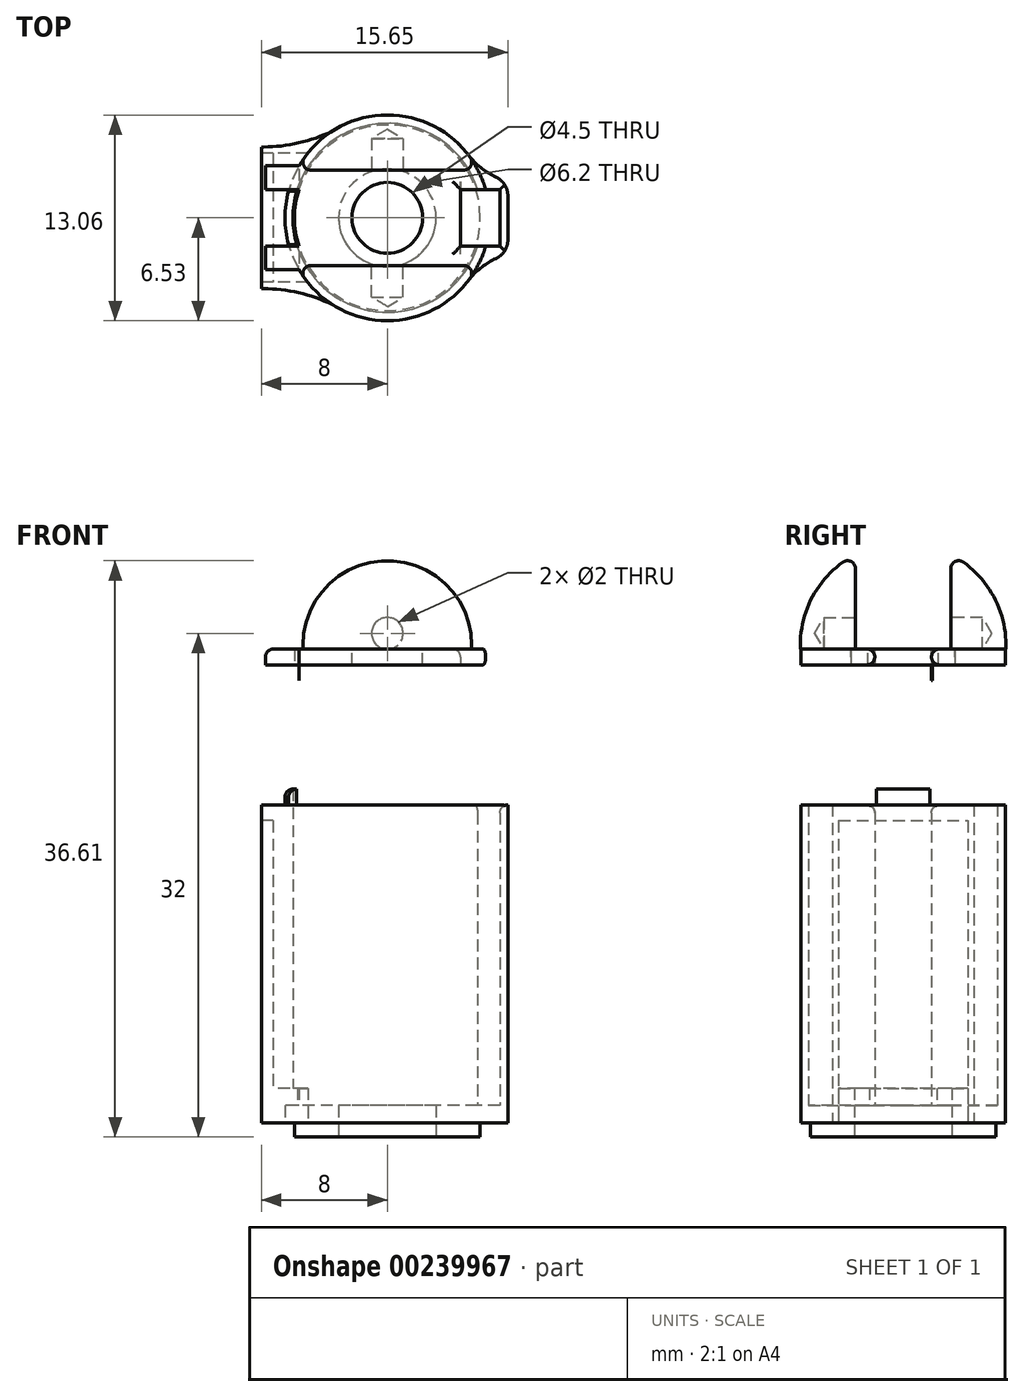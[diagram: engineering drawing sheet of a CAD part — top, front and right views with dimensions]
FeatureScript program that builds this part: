
annotation { "Feature Type Name" : "Feature", "Feature Type Description" : "" }
export const myFeature = defineFeature(function(context is Context, id is Id, definition is map)
    precondition{}
    {
        {
            var Q0;
            Q0=qCreatedBy(makeId("Top.planeOp"),FACE);
            var sketch = newSketch(context, id + "F0", { "sketchPlane" : qUnion([Q0])});
            skCircle(sketch, "E0", {"center": v(0, 0) * mm, "radius": 6 * mm});
            skLineSegment(sketch, "E1.bottom", {"start": v(7.15, 1.8) * mm, "end": v(3.35, 1.8) * mm});
            skLineSegment(sketch, "E1.top", {"start": v(7.15, -1.8) * mm, "end": v(3.35, -1.8) * mm});
            skLineSegment(sketch, "E1.left", {"start": v(7.15, 1.8) * mm, "end": v(7.15, -1.8) * mm});
            skLineSegment(sketch, "E1.right", {"start": v(3.35, 1.8) * mm, "end": v(3.35, -1.8) * mm});
            skCircle(sketch, "E2", {"center": v(0, 0) * mm, "radius": 6.5 * mm});
            skLineSegment(sketch, "E3", {"start": v(6.08, 2.3) * mm, "end": v(7.65, 2.3) * mm});
            skLineSegment(sketch, "E4", {"start": v(7.65, 2.3) * mm, "end": v(7.65, -2.3) * mm});
            skLineSegment(sketch, "E5", {"start": v(7.65, -2.3) * mm, "end": v(6.08, -2.3) * mm});
            skLineSegment(sketch, "E6", {"start": v(3.35, 1.8) * mm, "end": v(-6.25, 1.8) * mm, "construction": true});
            skLineSegment(sketch, "E7", {"start": v(3.35, -1.8) * mm, "end": v(-6.25, -1.8) * mm, "construction": true});
            skLineSegment(sketch, "E8", {"start": v(-6.25, 1.8) * mm, "end": v(-5.72, 1.8) * mm});
            skLineSegment(sketch, "E9", {"start": v(-6.25, -1.8) * mm, "end": v(-5.72, -1.8) * mm});
            skCircle(sketch, "E10", {"center": v(0, 0) * mm, "radius": 5.9 * mm});
            skSolve(sketch);
        }
        {
            var Q0;
            {var subQ2=sQuery(id+"F0.wireOp",EDGE,"E1.bottom");var subQ4=sQuery(id+"F0.wireOp",EDGE,"E0");var subQ5=makeQuery(id+"F0.imprint","INTERSECT",VERTEX,{"derivedFrom":[subQ4,subQ2]});Q0=makeQuery(id+"F0.imprint","IMPRINT",FACE,{"disambiguationData":[TD([[makeQuery(id+"F0.imprint","IMPRINT",EDGE,{"disambiguationData":[TD([[subQ5,-1.0]])],"derivedFrom":subQ4}),-1.0]])]});}
            var Q1;
            {var subQ4=sQuery(id+"F0.wireOp",EDGE,"E1.left");Q1=makeQuery(id+"F0.imprint","IMPRINT",FACE,{"disambiguationData":[TD([[makeQuery(id+"F0.imprint","IMPRINT",EDGE,{"derivedFrom":subQ4}),1.0]])]});}
            var Q2;
            {var subQ0=sQuery(id+"F0.wireOp",EDGE,"E8");Q2=makeQuery(id+"F0.imprint","IMPRINT",FACE,{"disambiguationData":[TD([[makeQuery(id+"F0.imprint","IMPRINT",EDGE,{"derivedFrom":subQ0}),-1.0]])]});}
            var Q3;
            {var subQ2=sQuery(id+"F0.wireOp",EDGE,"E9");Q3=makeQuery(id+"F0.imprint","IMPRINT",FACE,{"disambiguationData":[TD([[makeQuery(id+"F0.imprint","IMPRINT",EDGE,{"derivedFrom":subQ2}),-1.0]])]});}
            extrude(context, id + "F1", {"entities" : qUnion([Q0, Q1, Q2, Q3]), "depth" : 21.1 * mm});
        }
        {
            var Q0;
            {var subQ5=sQuery(id+"F0.wireOp",EDGE,"E1.right");Q0=makeQuery(id+"F0.imprint","IMPRINT",FACE,{"disambiguationData":[TD([[makeQuery(id+"F0.imprint","IMPRINT",EDGE,{"derivedFrom":subQ5}),-1.0]])]});}
            var Q1;
            {var subQ0=sQuery(id+"F0.wireOp",EDGE,"E1.left");Q1=makeQuery(id+"F0.imprint","IMPRINT",FACE,{"disambiguationData":[TD([[makeQuery(id+"F0.imprint","IMPRINT",EDGE,{"derivedFrom":subQ0}),-1.0]])]});}
            var Q2;
            {var subQ0=sQuery(id+"F0.wireOp",EDGE,"E1.bottom");var subQ1=sQuery(id+"F0.wireOp",EDGE,"E0");var subQ2=makeQuery(id+"F0.imprint","INTERSECT",VERTEX,{"derivedFrom":[subQ1,subQ0]});Q2=makeQuery(id+"F0.imprint","IMPRINT",FACE,{"disambiguationData":[TD([[makeQuery(id+"F0.imprint","IMPRINT",EDGE,{"disambiguationData":[TD([[subQ2,1.0]])],"derivedFrom":subQ1}),-1.0]])]});}
            var Q3;
            {var subQ5=sQuery(id+"F0.wireOp",EDGE,"E1.right");Q3=makeQuery(id+"F0.imprint","IMPRINT",FACE,{"disambiguationData":[TD([[makeQuery(id+"F0.imprint","IMPRINT",EDGE,{"derivedFrom":subQ5}),1.0]])]});}
            var Q4;
            {var subQ1=sQuery(id+"F0.wireOp",EDGE,"E0");var subQ8=makeQuery(id+"F0.imprint","INTERSECT",VERTEX,{"derivedFrom":[subQ1,sQuery(id+"F0.wireOp",EDGE,"E8")]});Q4=makeQuery(id+"F0.imprint","IMPRINT",FACE,{"disambiguationData":[TD([[makeQuery(id+"F0.imprint","IMPRINT",EDGE,{"disambiguationData":[TD([[subQ8,1.0]])],"derivedFrom":subQ1}),1.0]])]});}
            var Q5;
            {var subQ0=sQuery(id+"F0.wireOp",EDGE,"E1.bottom");var subQ1=sQuery(id+"F0.wireOp",EDGE,"E0");var subQ2=makeQuery(id+"F0.imprint","INTERSECT",VERTEX,{"derivedFrom":[subQ1,subQ0]});Q5=makeQuery(id+"F0.imprint","IMPRINT",FACE,{"disambiguationData":[TD([[makeQuery(id+"F0.imprint","IMPRINT",EDGE,{"disambiguationData":[TD([[subQ2,1.0]])],"derivedFrom":subQ1}),1.0]])]});}
            extrude(context, id + "F2", {"entities" : qUnion([Q0, Q1, Q2, Q3, Q4, Q5]), "operationType" : NewBodyOperationType.ADD, "depth" : 2 * mm});
        }
        {
            var Q0;
            {var subQ0=sQuery(id+"F0.wireOp",EDGE,"E1.left");Q0=makeQuery(id+"F0.imprint","IMPRINT",FACE,{"disambiguationData":[TD([[makeQuery(id+"F0.imprint","IMPRINT",EDGE,{"derivedFrom":subQ0}),-1.0]])]});}
            var Q1;
            {var subQ7=sQuery(id+"F0.wireOp",EDGE,"E1.left");Q1=makeQuery(id+"F0.imprint","IMPRINT",FACE,{"disambiguationData":[TD([[makeQuery(id+"F0.imprint","IMPRINT",EDGE,{"derivedFrom":subQ7}),1.0]])]});}
            extrude(context, id + "F3", {"entities" : qUnion([Q0, Q1]), "operationType" : NewBodyOperationType.REMOVE, "depth" : 0.9 * mm});
        }
        {
            var Q0;
            Q0=sQuery(id+"F0.wireOp",VERTEX,"E0.center");
            var Q1;
            Q1=makeQuery(id+"F1.opExtrude","SWEPT_BODY",BODY,{"disambiguationData":[OSD([sQuery(id+"F0.wireOp",EDGE,"E0"),sQuery(id+"F0.wireOp",EDGE,"4U9qkods-u3rM-atFx-P1sS-Y80TmgSaHfty.bottom"),sQuery(id+"F0.wireOp",EDGE,"4U9qkods-u3rM-atFx-P1sS-Y80TmgSaHfty.top"),sQuery(id+"F0.wireOp",EDGE,"4U9qkods-u3rM-atFx-P1sS-Y80TmgSaHfty.left"),sQuery(id+"F0.wireOp",EDGE,"4U9qkods-u3rM-atFx-P1sS-Y80TmgSaHfty.right"),sQuery(id+"F0.wireOp",EDGE,"mv0gvk0f-OwlG-QK1v-DSVR-qk8BXU6s7eKN"),sQuery(id+"F0.wireOp",EDGE,"3gOzF7jk-Ag0X-tEXh-jwYR-98HZdRz7N0tB"),sQuery(id+"F0.wireOp",EDGE,"9Uo2PhHU-4JkB-lCzV-Wcka-mTuiKmUsuITT")])]});
            hole(context, id + "F4", {"style" : HoleStyle.SIMPLE, "endStyle" : HoleEndStyle.THROUGH, "oppositeDirection" : true, "holeDiameter" : 6.2 * mm, "locations" : qUnion([Q0]), "scope" : qUnion([Q1]), "isTappedThrough" : true});
        }
        {
            var Q0;
            Q0=qCreatedBy(makeId("Top.planeOp"),FACE);
            cPlane(context, id + "F5", {"entities" : qUnion([Q0]), "cplaneType" : CPlaneType.OFFSET, "offset" : 30 * mm, "width" : 150 * mm, "height" : 150 * mm});
        }
        {
            var Q0;
            Q0=qCreatedBy(id+"F5.planeOp",FACE);
            var sketch = newSketch(context, id + "F6", { "sketchPlane" : qUnion([Q0])});
            skCircle(sketch, "E11", {"center": v(0, 0) * mm, "radius": 5.9 * mm});
            skCircle(sketch, "E12", {"center": v(0, 0) * mm, "radius": 6.5 * mm});
            skLineSegment(sketch, "E13", {"start": v(4.65, 1.8) * mm, "end": v(6.25, 1.8) * mm});
            skLineSegment(sketch, "E14", {"start": v(4.65, -1.8) * mm, "end": v(6.25, -1.8) * mm});
            skLineSegment(sketch, "E15", {"start": v(7.15, 1.8) * mm, "end": v(-6.25, 1.8) * mm, "construction": true});
            skLineSegment(sketch, "E16", {"start": v(7.15, -1.8) * mm, "end": v(-6.25, -1.8) * mm, "construction": true});
            skLineSegment(sketch, "E17", {"start": v(-6.25, 1.8) * mm, "end": v(-5.62, 1.8) * mm});
            skLineSegment(sketch, "E18", {"start": v(-6.25, -1.8) * mm, "end": v(-5.62, -1.8) * mm});
            skLineSegment(sketch, "E19", {"start": v(4.65, 1.8) * mm, "end": v(4.65, -1.8) * mm});
            skCircle(sketch, "E20", {"center": v(0, 0) * mm, "radius": 4.5 * mm});
            skLineSegment(sketch, "E21.bottom", {"start": v(-7.75, 1.8) * mm, "end": v(-6.25, 1.8) * mm});
            skLineSegment(sketch, "E21.top", {"start": v(-7.75, -1.8) * mm, "end": v(-6.25, -1.8) * mm});
            skLineSegment(sketch, "E21.left", {"start": v(-7.75, 1.8) * mm, "end": v(-7.75, -1.8) * mm});
            skLineSegment(sketch, "E21.right", {"start": v(-6.25, 1.8) * mm, "end": v(-6.25, -1.8) * mm});
            skLineSegment(sketch, "E22.bottom", {"start": v(-7.75, 1.8) * mm, "end": v(-5.6, 1.8) * mm});
            skLineSegment(sketch, "E22.top", {"start": v(-7.75, 3.3) * mm, "end": v(-5.6, 3.3) * mm});
            skLineSegment(sketch, "E22.left", {"start": v(-7.75, 1.8) * mm, "end": v(-7.75, 3.3) * mm});
            skLineSegment(sketch, "E22.right", {"start": v(-5.6, 1.8) * mm, "end": v(-5.6, 3.3) * mm});
            skLineSegment(sketch, "E23.bottom", {"start": v(-7.75, -1.8) * mm, "end": v(-5.6, -1.8) * mm});
            skLineSegment(sketch, "E23.top", {"start": v(-7.75, -3.3) * mm, "end": v(-5.6, -3.3) * mm});
            skLineSegment(sketch, "E23.left", {"start": v(-7.75, -1.8) * mm, "end": v(-7.75, -3.3) * mm});
            skLineSegment(sketch, "E23.right", {"start": v(-5.6, -1.8) * mm, "end": v(-5.6, -3.3) * mm});
            skSolve(sketch);
        }
        {
            var Q0;
            {var subQ0=sQuery(id+"F6.wireOp",EDGE,"E22.right");var subQ1=sQuery(id+"F6.wireOp",EDGE,"E11");var subQ2=makeQuery(id+"F6.imprint","INTERSECT",VERTEX,{"derivedFrom":[subQ1,subQ0]});Q0=makeQuery(id+"F6.imprint","IMPRINT",FACE,{"disambiguationData":[TD([[makeQuery(id+"F6.imprint","IMPRINT",EDGE,{"disambiguationData":[TD([[subQ2,1.0]])],"derivedFrom":subQ1}),-1.0]])]});}
            var Q1;
            {var subQ0=sQuery(id+"F6.wireOp",EDGE,"E23.right");var subQ1=sQuery(id+"F6.wireOp",EDGE,"E11");var subQ2=makeQuery(id+"F6.imprint","INTERSECT",VERTEX,{"derivedFrom":[subQ1,subQ0]});Q1=makeQuery(id+"F6.imprint","IMPRINT",FACE,{"disambiguationData":[TD([[makeQuery(id+"F6.imprint","IMPRINT",EDGE,{"disambiguationData":[TD([[subQ2,-1.0]])],"derivedFrom":subQ1}),-1.0]])]});}
            var Q2;
            {var subQ0=sQuery(id+"F6.wireOp",EDGE,"E22.right");var subQ1=sQuery(id+"F6.wireOp",EDGE,"E11");var subQ2=makeQuery(id+"F6.imprint","INTERSECT",VERTEX,{"derivedFrom":[subQ1,subQ0]});Q2=makeQuery(id+"F6.imprint","IMPRINT",FACE,{"disambiguationData":[TD([[makeQuery(id+"F6.imprint","IMPRINT",EDGE,{"disambiguationData":[TD([[subQ2,-1.0]])],"derivedFrom":subQ1}),-1.0]])]});}
            var Q3;
            {var subQ0=sQuery(id+"F6.wireOp",EDGE,"E23.bottom");var subQ1=sQuery(id+"F6.wireOp",EDGE,"E11");var subQ2=makeQuery(id+"F6.imprint","INTERSECT",VERTEX,{"derivedFrom":[subQ1,subQ0]});Q3=makeQuery(id+"F6.imprint","IMPRINT",FACE,{"disambiguationData":[TD([[makeQuery(id+"F6.imprint","IMPRINT",EDGE,{"disambiguationData":[TD([[subQ2,-1.0]])],"derivedFrom":subQ1}),-1.0]])]});}
            var Q4;
            {var subQ0=sQuery(id+"F6.wireOp",EDGE,"E22.right");var subQ1=sQuery(id+"F6.wireOp",EDGE,"E11");var subQ2=makeQuery(id+"F6.imprint","INTERSECT",VERTEX,{"derivedFrom":[subQ1,subQ0]});Q4=makeQuery(id+"F6.imprint","IMPRINT",FACE,{"disambiguationData":[TD([[makeQuery(id+"F6.imprint","IMPRINT",EDGE,{"disambiguationData":[TD([[subQ2,1.0]])],"derivedFrom":subQ1}),-1.0]])]});}
            var Q5;
            {var subQ0=sQuery(id+"F6.wireOp",EDGE,"E23.right");var subQ1=sQuery(id+"F6.wireOp",EDGE,"E11");var subQ2=makeQuery(id+"F6.imprint","INTERSECT",VERTEX,{"derivedFrom":[subQ1,subQ0]});Q5=makeQuery(id+"F6.imprint","IMPRINT",FACE,{"disambiguationData":[TD([[makeQuery(id+"F6.imprint","IMPRINT",EDGE,{"disambiguationData":[TD([[subQ2,-1.0]])],"derivedFrom":subQ1}),-1.0]])]});}
            var Q6;
            {var subQ0=sQuery(id+"F6.wireOp",EDGE,"E22.right");var subQ1=sQuery(id+"F6.wireOp",EDGE,"E11");var subQ2=makeQuery(id+"F6.imprint","INTERSECT",VERTEX,{"derivedFrom":[subQ1,subQ0]});Q6=makeQuery(id+"F6.imprint","IMPRINT",FACE,{"disambiguationData":[TD([[makeQuery(id+"F6.imprint","IMPRINT",EDGE,{"disambiguationData":[TD([[subQ2,-1.0]])],"derivedFrom":subQ1}),-1.0]])]});}
            var Q7;
            {var subQ0=sQuery(id+"F6.wireOp",EDGE,"E23.bottom");var subQ1=sQuery(id+"F6.wireOp",EDGE,"E11");var subQ2=makeQuery(id+"F6.imprint","INTERSECT",VERTEX,{"derivedFrom":[subQ1,subQ0]});Q7=makeQuery(id+"F6.imprint","IMPRINT",FACE,{"disambiguationData":[TD([[makeQuery(id+"F6.imprint","IMPRINT",EDGE,{"disambiguationData":[TD([[subQ2,-1.0]])],"derivedFrom":subQ1}),-1.0]])]});}
            var Q8;
            {var subQ5=sQuery(id+"F6.wireOp",EDGE,"E19");Q8=makeQuery(id+"F6.imprint","IMPRINT",FACE,{"disambiguationData":[TD([[makeQuery(id+"F6.imprint","IMPRINT",EDGE,{"derivedFrom":subQ5}),-1.0]])]});}
            var Q9;
            {var subQ5=sQuery(id+"F6.wireOp",EDGE,"E19");Q9=makeQuery(id+"F6.imprint","IMPRINT",FACE,{"disambiguationData":[TD([[makeQuery(id+"F6.imprint","IMPRINT",EDGE,{"derivedFrom":subQ5}),-1.0]])]});}
            var Q10;
            {var subQ5=sQuery(id+"F6.wireOp",EDGE,"E19");Q10=makeQuery(id+"F6.imprint","IMPRINT",FACE,{"disambiguationData":[TD([[makeQuery(id+"F6.imprint","IMPRINT",EDGE,{"derivedFrom":subQ5}),-1.0]])]});}
            var Q11;
            {var subQ5=sQuery(id+"F6.wireOp",EDGE,"E19");Q11=makeQuery(id+"F6.imprint","IMPRINT",FACE,{"disambiguationData":[TD([[makeQuery(id+"F6.imprint","IMPRINT",EDGE,{"derivedFrom":subQ5}),-1.0]])]});}
            var Q12;
            {var subQ5=sQuery(id+"F6.wireOp",EDGE,"E19");Q12=makeQuery(id+"F6.imprint","IMPRINT",FACE,{"disambiguationData":[TD([[makeQuery(id+"F6.imprint","IMPRINT",EDGE,{"derivedFrom":subQ5}),-1.0]])]});}
            var Q13;
            Q13=makeQuery(id+"F6.imprint","IMPRINT",FACE,{"disambiguationData":[TD([[makeQuery(id+"F6.imprint","IMPRINT",EDGE,{"derivedFrom":sQuery(id+"F6.wireOp",EDGE,"E20")}),1.0]])]});
            var Q14;
            {var subQ0=sQuery(id+"F6.wireOp",EDGE,"E22.right");var subQ1=sQuery(id+"F6.wireOp",EDGE,"E11");var subQ2=makeQuery(id+"F6.imprint","INTERSECT",VERTEX,{"derivedFrom":[subQ1,subQ0]});Q14=makeQuery(id+"F6.imprint","IMPRINT",FACE,{"disambiguationData":[TD([[makeQuery(id+"F6.imprint","IMPRINT",EDGE,{"disambiguationData":[TD([[subQ2,1.0]])],"derivedFrom":subQ1}),-1.0]])]});}
            var Q15;
            {var subQ0=sQuery(id+"F6.wireOp",EDGE,"E23.right");var subQ1=sQuery(id+"F6.wireOp",EDGE,"E11");var subQ2=makeQuery(id+"F6.imprint","INTERSECT",VERTEX,{"derivedFrom":[subQ1,subQ0]});Q15=makeQuery(id+"F6.imprint","IMPRINT",FACE,{"disambiguationData":[TD([[makeQuery(id+"F6.imprint","IMPRINT",EDGE,{"disambiguationData":[TD([[subQ2,-1.0]])],"derivedFrom":subQ1}),-1.0]])]});}
            var Q16;
            {var subQ0=sQuery(id+"F6.wireOp",EDGE,"E22.right");var subQ1=sQuery(id+"F6.wireOp",EDGE,"E11");var subQ2=makeQuery(id+"F6.imprint","INTERSECT",VERTEX,{"derivedFrom":[subQ1,subQ0]});Q16=makeQuery(id+"F6.imprint","IMPRINT",FACE,{"disambiguationData":[TD([[makeQuery(id+"F6.imprint","IMPRINT",EDGE,{"disambiguationData":[TD([[subQ2,-1.0]])],"derivedFrom":subQ1}),-1.0]])]});}
            var Q17;
            {var subQ0=sQuery(id+"F6.wireOp",EDGE,"E23.bottom");var subQ1=sQuery(id+"F6.wireOp",EDGE,"E11");var subQ2=makeQuery(id+"F6.imprint","INTERSECT",VERTEX,{"derivedFrom":[subQ1,subQ0]});Q17=makeQuery(id+"F6.imprint","IMPRINT",FACE,{"disambiguationData":[TD([[makeQuery(id+"F6.imprint","IMPRINT",EDGE,{"disambiguationData":[TD([[subQ2,-1.0]])],"derivedFrom":subQ1}),-1.0]])]});}
            var Q18;
            {var subQ3=sQuery(id+"F6.wireOp",EDGE,"E22.top");Q18=makeQuery(id+"F6.imprint","IMPRINT",FACE,{"disambiguationData":[TD([[makeQuery(id+"F6.imprint","IMPRINT",EDGE,{"derivedFrom":subQ3}),-1.0]])]});}
            var Q19;
            {var subQ0=sQuery(id+"F6.wireOp",EDGE,"E22.right");var subQ1=sQuery(id+"F6.wireOp",EDGE,"E11");var subQ2=makeQuery(id+"F6.imprint","INTERSECT",VERTEX,{"derivedFrom":[subQ1,subQ0]});Q19=makeQuery(id+"F6.imprint","IMPRINT",FACE,{"disambiguationData":[TD([[makeQuery(id+"F6.imprint","IMPRINT",EDGE,{"disambiguationData":[TD([[subQ2,1.0]])],"derivedFrom":subQ1}),-1.0]])]});}
            var Q20;
            {var subQ0=sQuery(id+"F6.wireOp",EDGE,"E22.right");var subQ1=sQuery(id+"F6.wireOp",EDGE,"E11");var subQ2=makeQuery(id+"F6.imprint","INTERSECT",VERTEX,{"derivedFrom":[subQ1,subQ0]});Q20=makeQuery(id+"F6.imprint","IMPRINT",FACE,{"disambiguationData":[TD([[makeQuery(id+"F6.imprint","IMPRINT",EDGE,{"disambiguationData":[TD([[subQ2,-1.0]])],"derivedFrom":subQ1}),-1.0]])]});}
            var Q21;
            {var subQ0=sQuery(id+"F6.wireOp",EDGE,"E23.bottom");var subQ1=sQuery(id+"F6.wireOp",EDGE,"E11");var subQ2=makeQuery(id+"F6.imprint","INTERSECT",VERTEX,{"derivedFrom":[subQ1,subQ0]});Q21=makeQuery(id+"F6.imprint","IMPRINT",FACE,{"disambiguationData":[TD([[makeQuery(id+"F6.imprint","IMPRINT",EDGE,{"disambiguationData":[TD([[subQ2,-1.0]])],"derivedFrom":subQ1}),-1.0]])]});}
            var Q22;
            {var subQ0=sQuery(id+"F6.wireOp",EDGE,"E23.right");var subQ1=sQuery(id+"F6.wireOp",EDGE,"E11");var subQ2=makeQuery(id+"F6.imprint","INTERSECT",VERTEX,{"derivedFrom":[subQ1,subQ0]});Q22=makeQuery(id+"F6.imprint","IMPRINT",FACE,{"disambiguationData":[TD([[makeQuery(id+"F6.imprint","IMPRINT",EDGE,{"disambiguationData":[TD([[subQ2,-1.0]])],"derivedFrom":subQ1}),-1.0]])]});}
            var Q23;
            {var subQ3=sQuery(id+"F6.wireOp",EDGE,"E23.top");Q23=makeQuery(id+"F6.imprint","IMPRINT",FACE,{"disambiguationData":[TD([[makeQuery(id+"F6.imprint","IMPRINT",EDGE,{"derivedFrom":subQ3}),1.0]])]});}
            var Q24;
            {var subQ0=sQuery(id+"F6.wireOp",EDGE,"E22.right");var subQ1=sQuery(id+"F6.wireOp",EDGE,"E11");var subQ2=makeQuery(id+"F6.imprint","INTERSECT",VERTEX,{"derivedFrom":[subQ1,subQ0]});Q24=makeQuery(id+"F6.imprint","IMPRINT",FACE,{"disambiguationData":[TD([[makeQuery(id+"F6.imprint","IMPRINT",EDGE,{"disambiguationData":[TD([[subQ2,-1.0]])],"derivedFrom":subQ1}),1.0]])]});}
            var Q25;
            {var subQ0=sQuery(id+"F6.wireOp",EDGE,"E23.bottom");var subQ1=sQuery(id+"F6.wireOp",EDGE,"E11");var subQ2=makeQuery(id+"F6.imprint","INTERSECT",VERTEX,{"derivedFrom":[subQ1,subQ0]});Q25=makeQuery(id+"F6.imprint","IMPRINT",FACE,{"disambiguationData":[TD([[makeQuery(id+"F6.imprint","IMPRINT",EDGE,{"disambiguationData":[TD([[subQ2,-1.0]])],"derivedFrom":subQ1}),1.0]])]});}
            extrude(context, id + "F7", {"entities" : qUnion([Q0, Q1, Q2, Q3, Q4, Q5, Q6, Q7, Q8, Q9, Q10, Q11, Q12, Q13, Q14, Q15, Q16, Q17, Q18, Q19, Q20, Q21, Q22, Q23, Q24, Q25]), "depth" : 1 * mm});
        }
        {
            var Q0;
            {var subQ0=sQuery(id+"F6.wireOp",EDGE,"4l1vRjtD-Y7ke-iHX6-YueY-vymgdgJSGHIw");Q0=makeQuery(id+"F6.imprint","IMPRINT",FACE,{"disambiguationData":[TD([[makeQuery(id+"F6.imprint","IMPRINT",EDGE,{"derivedFrom":subQ0}),-1.0]])]});}
            var Q1;
            {var subQ1=sQuery(id+"F6.wireOp",EDGE,"E11");var subQ9=makeQuery(id+"F6.imprint","INTERSECT",VERTEX,{"derivedFrom":[subQ1,sQuery(id+"F6.wireOp",EDGE,"E17")]});Q1=makeQuery(id+"F6.imprint","IMPRINT",FACE,{"disambiguationData":[TD([[makeQuery(id+"F6.imprint","IMPRINT",EDGE,{"disambiguationData":[TD([[subQ9,1.0]])],"derivedFrom":subQ1}),1.0]])]});}
            extrude(context, id + "F8", {"entities" : qUnion([Q0, Q1]), "operationType" : NewBodyOperationType.ADD, "oppositeDirection" : true, "depth" : 1 * mm});
        }
        {
            var Q0;
            Q0=makeQuery(id+"F7.opExtrude","CAP_FACE",FACE,{"disambiguationData":[OSD([sQuery(id+"F6.wireOp",EDGE,"E12")])],"isStart":false});
            var sketch = newSketch(context, id + "F9", { "sketchPlane" : qUnion([Q0])});
            skPoint(sketch, "E24", {"position": v(0, 0) * mm});
            skLineSegment(sketch, "E25.bottom", {"start": v(-5.75, 6.53) * mm, "end": v(5.75, 6.53) * mm});
            skLineSegment(sketch, "E25.top", {"start": v(-5.75, 3.03) * mm, "end": v(5.75, 3.03) * mm});
            skLineSegment(sketch, "E25.left", {"start": v(-5.75, 6.53) * mm, "end": v(-5.75, 3.03) * mm});
            skLineSegment(sketch, "E25.right", {"start": v(5.75, 6.53) * mm, "end": v(5.75, 3.03) * mm});
            skLineSegment(sketch, "E26", {"start": v(0, 6.56) * mm, "end": v(0, -6.53) * mm, "construction": true});
            skPoint(sketch, "E27", {"position": v(0, 3.03) * mm});
            skLineSegment(sketch, "E28.MirrorCS", {"start": v(-5.75, -6.53) * mm, "end": v(5.75, -6.53) * mm});
            skLineSegment(sketch, "E29.MirrorCS", {"start": v(-5.75, -3.03) * mm, "end": v(5.75, -3.03) * mm});
            skLineSegment(sketch, "E30.MirrorCS", {"start": v(-5.75, -6.53) * mm, "end": v(-5.75, -3.03) * mm});
            skLineSegment(sketch, "E31.MirrorCS", {"start": v(5.75, -6.53) * mm, "end": v(5.75, -3.03) * mm});
            skSolve(sketch);
        }
        {
            var Q0;
            Q0=sQuery(id+"F9.wireOp",VERTEX,"E24");
            var Q1;
            Q1=makeQuery(id+"F7.opExtrude","SWEPT_BODY",BODY,{"disambiguationData":[OSD([sQuery(id+"F6.wireOp",EDGE,"E12")])]});
            hole(context, id + "F10", {"style" : HoleStyle.SIMPLE, "endStyle" : HoleEndStyle.THROUGH, "holeDiameter" : 4.5 * mm, "locations" : qUnion([Q0]), "scope" : qUnion([Q1]), "isTappedThrough" : true});
        }
        {
            var Q0;
            Q0=makeQuery(id+"F1.opExtrude","CAP_FACE",FACE,{"disambiguationData":[OSD([sQuery(id+"F0.wireOp",EDGE,"E0"),sQuery(id+"F0.wireOp",EDGE,"E1.bottom"),sQuery(id+"F0.wireOp",EDGE,"E1.top"),sQuery(id+"F0.wireOp",EDGE,"E1.left"),sQuery(id+"F0.wireOp",EDGE,"E2"),sQuery(id+"F0.wireOp",EDGE,"E3"),sQuery(id+"F0.wireOp",EDGE,"E4"),sQuery(id+"F0.wireOp",EDGE,"E5")])],"isStart":false});
            var sketch = newSketch(context, id + "F11", { "sketchPlane" : qUnion([Q0])});
            skLineSegment(sketch, "E32", {"start": v(-6.27, 1.7) * mm, "end": v(-5.75, 1.7) * mm});
            skArc(sketch, "E33", {"start": v(-6.27, 1.7) * mm, "mid": v(-6.5, 0) * mm, "end": v(-6.27, -1.7) * mm});
            skArc(sketch, "E34", {"start": v(-5.75, 1.7) * mm, "mid": v(-6, 0) * mm, "end": v(-5.75, -1.7) * mm});
            skLineSegment(sketch, "E35", {"start": v(-6.27, -1.7) * mm, "end": v(-5.75, -1.7) * mm});
            skLineSegment(sketch, "E36", {"start": v(7.15, 1.8) * mm, "end": v(7.15, 2.3) * mm});
            skLineSegment(sketch, "E37", {"start": v(7.15, -1.8) * mm, "end": v(7.15, -2.3) * mm});
            skSolve(sketch);
        }
        {
            var Q0;
            Q0=makeQuery(id+"F11.imprint","IMPRINT",FACE,{"disambiguationData":[TD([[makeQuery(id+"F11.imprint","IMPRINT",EDGE,{"derivedFrom":sQuery(id+"F11.wireOp",EDGE,"E32")}),-1.0]])]});
            extrude(context, id + "F12", {"entities" : qUnion([Q0]), "operationType" : NewBodyOperationType.ADD, "depth" : 1 * mm});
        }
        {
            var Q0;
            {var subQ1=sQuery(id+"F9.wireOp",EDGE,"E25.top");Q0=makeQuery(id+"F9.imprint","IMPRINT",FACE,{"disambiguationData":[TD([[makeQuery(id+"F9.imprint","IMPRINT",EDGE,{"derivedFrom":subQ1}),1.0]])]});}
            var Q1;
            {var subQ1=sQuery(id+"F9.wireOp",EDGE,"E29.MirrorCS");Q1=makeQuery(id+"F9.imprint","IMPRINT",FACE,{"disambiguationData":[TD([[makeQuery(id+"F9.imprint","IMPRINT",EDGE,{"derivedFrom":subQ1}),-1.0]])]});}
            var Q2;
            {var subQ0=sQuery(id+"F9.wireOp",EDGE,"E30.MirrorCS");var subQ1=sQuery(id+"F9.wireOp",EDGE,"E28.MirrorCS");var subQ2=makeQuery(id+"F9.imprint","INTERSECT",VERTEX,{"derivedFrom":[subQ1,subQ0]});Q2=makeQuery(id+"F9.imprint","IMPRINT",FACE,{"disambiguationData":[TD([[makeQuery(id+"F9.imprint","IMPRINT",EDGE,{"disambiguationData":[TD([[subQ2,-1.0]])],"derivedFrom":subQ1}),1.0]])]});}
            var Q3;
            {var subQ0=sQuery(id+"F9.wireOp",EDGE,"E31.MirrorCS");var subQ1=sQuery(id+"F9.wireOp",EDGE,"E28.MirrorCS");var subQ2=makeQuery(id+"F9.imprint","INTERSECT",VERTEX,{"derivedFrom":[subQ1,subQ0]});Q3=makeQuery(id+"F9.imprint","IMPRINT",FACE,{"disambiguationData":[TD([[makeQuery(id+"F9.imprint","IMPRINT",EDGE,{"disambiguationData":[TD([[subQ2,1.0]])],"derivedFrom":subQ1}),1.0]])]});}
            var Q4;
            {var subQ0=sQuery(id+"F9.wireOp",EDGE,"E25.right");var subQ1=sQuery(id+"F9.wireOp",EDGE,"E25.bottom");var subQ2=makeQuery(id+"F9.imprint","INTERSECT",VERTEX,{"derivedFrom":[subQ1,subQ0]});Q4=makeQuery(id+"F9.imprint","IMPRINT",FACE,{"disambiguationData":[TD([[makeQuery(id+"F9.imprint","IMPRINT",EDGE,{"disambiguationData":[TD([[subQ2,1.0]])],"derivedFrom":subQ1}),-1.0]])]});}
            var Q5;
            {var subQ0=sQuery(id+"F9.wireOp",EDGE,"E25.left");var subQ1=sQuery(id+"F9.wireOp",EDGE,"E25.bottom");var subQ2=makeQuery(id+"F9.imprint","INTERSECT",VERTEX,{"derivedFrom":[subQ1,subQ0]});Q5=makeQuery(id+"F9.imprint","IMPRINT",FACE,{"disambiguationData":[TD([[makeQuery(id+"F9.imprint","IMPRINT",EDGE,{"disambiguationData":[TD([[subQ2,-1.0]])],"derivedFrom":subQ1}),-1.0]])]});}
            extrude(context, id + "F13", {"entities" : qUnion([Q0, Q1, Q2, Q3, Q4, Q5]), "operationType" : NewBodyOperationType.ADD, "depth" : 6 * mm});
        }
        {
            var Q0;
            Q0=makeQuery(id+"F13.opExtrude","CAP_EDGE",EDGE,{"disambiguationData":[OSD([sQuery(id+"F9.wireOp",EDGE,"E30.MirrorCS")])],"isStart":false});
            var Q1;
            Q1=makeQuery(id+"F13.opExtrude","CAP_EDGE",EDGE,{"disambiguationData":[OSD([sQuery(id+"F9.wireOp",EDGE,"E31.MirrorCS")])],"isStart":false});
            var Q2;
            Q2=makeQuery(id+"F13.opExtrude","CAP_EDGE",EDGE,{"disambiguationData":[OSD([sQuery(id+"F9.wireOp",EDGE,"E25.left")])],"isStart":false});
            var Q3;
            Q3=makeQuery(id+"F13.opExtrude","CAP_EDGE",EDGE,{"disambiguationData":[OSD([sQuery(id+"F9.wireOp",EDGE,"E25.right")])],"isStart":false});
            fillet(context, id + "F14", {"entities" : qUnion([Q0, Q1, Q2, Q3]), "radius" : 5.75 * mm, "tangentPropagation" : true, "allowEdgeOverflow" : false});
        }
        {
            var Q0;
            Q0=makeQuery(id+"F13.opExtrude","SWEPT_FACE",FACE,{"disambiguationData":[OSD([sQuery(id+"F9.wireOp",EDGE,"E28.MirrorCS")])]});
            var sketch = newSketch(context, id + "F15", { "sketchPlane" : qUnion([Q0])});
            skPoint(sketch, "E38", {"position": v(0, 32) * mm});
            skCircle(sketch, "E39", {"center": v(0, 32) * mm, "radius": 1 * mm, "construction": true});
            skSolve(sketch);
        }
        {
            var Q0;
            Q0=makeQuery(id+"F1.opExtrude","SWEPT_EDGE",EDGE,{"disambiguationData":[OSD([sQuery(id+"F0.wireOp",EDGE,"E2"),sQuery(id+"F0.wireOp",EDGE,"E5")])]});
            var Q1;
            Q1=makeQuery(id+"F1.opExtrude","SWEPT_EDGE",EDGE,{"disambiguationData":[OSD([sQuery(id+"F0.wireOp",EDGE,"E2"),sQuery(id+"F0.wireOp",EDGE,"E3")])]});
            fillet(context, id + "F16", {"entities" : qUnion([Q0, Q1]), "radius" : 5 * mm, "allowEdgeOverflow" : false});
        }
        {
            var Q0;
            {var subQ2=sQuery(id+"F0.wireOp",EDGE,"E8");Q0=makeQuery(id+"F0.imprint","IMPRINT",FACE,{"disambiguationData":[TD([[makeQuery(id+"F0.imprint","IMPRINT",EDGE,{"derivedFrom":subQ2}),1.0]])]});}
            var Q1;
            {var subQ0=sQuery(id+"F0.wireOp",EDGE,"E8");Q1=makeQuery(id+"F0.imprint","IMPRINT",FACE,{"disambiguationData":[TD([[makeQuery(id+"F0.imprint","IMPRINT",EDGE,{"derivedFrom":subQ0}),-1.0]])]});}
            var Q2;
            {var subQ2=sQuery(id+"F0.wireOp",EDGE,"E9");Q2=makeQuery(id+"F0.imprint","IMPRINT",FACE,{"disambiguationData":[TD([[makeQuery(id+"F0.imprint","IMPRINT",EDGE,{"derivedFrom":subQ2}),-1.0]])]});}
            var Q3;
            {var subQ0=sQuery(id+"F0.wireOp",EDGE,"E1.bottom");var subQ1=sQuery(id+"F0.wireOp",EDGE,"E0");var subQ2=makeQuery(id+"F0.imprint","INTERSECT",VERTEX,{"derivedFrom":[subQ1,subQ0]});Q3=makeQuery(id+"F0.imprint","IMPRINT",FACE,{"disambiguationData":[TD([[makeQuery(id+"F0.imprint","IMPRINT",EDGE,{"disambiguationData":[TD([[subQ2,1.0]])],"derivedFrom":subQ1}),-1.0]])]});}
            var Q4;
            {var subQ1=sQuery(id+"F0.wireOp",EDGE,"E0");var subQ8=makeQuery(id+"F0.imprint","INTERSECT",VERTEX,{"derivedFrom":[subQ1,sQuery(id+"F0.wireOp",EDGE,"E8")]});Q4=makeQuery(id+"F0.imprint","IMPRINT",FACE,{"disambiguationData":[TD([[makeQuery(id+"F0.imprint","IMPRINT",EDGE,{"disambiguationData":[TD([[subQ8,1.0]])],"derivedFrom":subQ1}),1.0]])]});}
            var Q5;
            {var subQ0=sQuery(id+"F0.wireOp",EDGE,"E1.bottom");var subQ1=sQuery(id+"F0.wireOp",EDGE,"E0");var subQ2=makeQuery(id+"F0.imprint","INTERSECT",VERTEX,{"derivedFrom":[subQ1,subQ0]});Q5=makeQuery(id+"F0.imprint","IMPRINT",FACE,{"disambiguationData":[TD([[makeQuery(id+"F0.imprint","IMPRINT",EDGE,{"disambiguationData":[TD([[subQ2,1.0]])],"derivedFrom":subQ1}),1.0]])]});}
            extrude(context, id + "F17", {"entities" : qUnion([Q0, Q1, Q2, Q3, Q4, Q5]), "operationType" : NewBodyOperationType.REMOVE, "depth" : 0.9 * mm});
        }
        {
            var Q0;
            Q0=makeQuery(id+"F16.opFillet","BLEND_EDGE",EDGE,{"blendedFrom":[makeQuery(id+"F1.opExtrude","SWEPT_EDGE",EDGE,{"disambiguationData":[OSD([sQuery(id+"F0.wireOp",EDGE,"E2"),sQuery(id+"F0.wireOp",EDGE,"E5")])]}),makeQuery(id+"F1.opExtrude","SWEPT_FACE",FACE,{"disambiguationData":[OSD([sQuery(id+"F0.wireOp",EDGE,"E4")])]})],"blendedInto":[makeQuery(id+"F1.opExtrude","SWEPT_FACE",FACE,{"disambiguationData":[OSD([sQuery(id+"F0.wireOp",EDGE,"E4")])]})]});
            var Q1;
            Q1=makeQuery(id+"F16.opFillet","BLEND_EDGE",EDGE,{"blendedFrom":[makeQuery(id+"F1.opExtrude","SWEPT_EDGE",EDGE,{"disambiguationData":[OSD([sQuery(id+"F0.wireOp",EDGE,"E2"),sQuery(id+"F0.wireOp",EDGE,"E3")])]}),makeQuery(id+"F1.opExtrude","SWEPT_FACE",FACE,{"disambiguationData":[OSD([sQuery(id+"F0.wireOp",EDGE,"E4")])]})],"blendedInto":[makeQuery(id+"F1.opExtrude","SWEPT_FACE",FACE,{"disambiguationData":[OSD([sQuery(id+"F0.wireOp",EDGE,"E4")])]})]});
            fillet(context, id + "F18", {"entities" : qUnion([Q0, Q1]), "radius" : 1.3 * mm, "tangentPropagation" : true, "allowEdgeOverflow" : false});
        }
        {
            var Q0;
            Q0=qCreatedBy(makeId("Right.planeOp"),FACE);
            cPlane(context, id + "F19", {"entities" : qUnion([Q0]), "cplaneType" : CPlaneType.OFFSET, "offset" : 8 * mm, "oppositeDirection" : true, "width" : 150 * mm, "height" : 150 * mm});
        }
        {
            var Q0;
            Q0=qCreatedBy(id+"F19.planeOp",FACE);
            var sketch = newSketch(context, id + "F20", { "sketchPlane" : qUnion([Q0])});
            skLineSegment(sketch, "E40.bottom", {"start": v(4.1, 20.1) * mm, "end": v(-4.1, 20.1) * mm});
            skLineSegment(sketch, "E40.top", {"start": v(4.1, 0.9) * mm, "end": v(-4.1, 0.9) * mm});
            skLineSegment(sketch, "E40.left", {"start": v(4.1, 20.1) * mm, "end": v(4.1, 0.9) * mm});
            skLineSegment(sketch, "E40.right", {"start": v(-4.1, 20.1) * mm, "end": v(-4.1, 0.9) * mm});
            skPoint(sketch, "E41", {"position": v(0, 20.1) * mm});
            skLineSegment(sketch, "E42", {"start": v(0, 40.2) * mm, "end": v(0, 0) * mm, "construction": true});
            skLineSegment(sketch, "E43.bottom", {"start": v(4.5, 21.1) * mm, "end": v(-4.5, 21.1) * mm});
            skLineSegment(sketch, "E43.top", {"start": v(4.5, 0.9) * mm, "end": v(-4.5, 0.9) * mm});
            skLineSegment(sketch, "E43.left", {"start": v(4.5, 21.1) * mm, "end": v(4.5, 0.9) * mm});
            skLineSegment(sketch, "E43.right", {"start": v(-4.5, 21.1) * mm, "end": v(-4.5, 0.9) * mm});
            skLineSegment(sketch, "E44.bottom", {"start": v(3.1, 2) * mm, "end": v(-3.1, 2) * mm});
            skLineSegment(sketch, "E44.top", {"start": v(3.1, 20.1) * mm, "end": v(-3.1, 20.1) * mm});
            skLineSegment(sketch, "E44.left", {"start": v(3.1, 2) * mm, "end": v(3.1, 20.1) * mm});
            skLineSegment(sketch, "E44.right", {"start": v(-3.1, 2) * mm, "end": v(-3.1, 20.1) * mm});
            skLineSegment(sketch, "E45.top", {"start": v(4.1, 3.1) * mm, "end": v(-4.1, 3.1) * mm});
            skLineSegment(sketch, "E45.left", {"start": v(4.1, 0.9) * mm, "end": v(4.1, 3.1) * mm});
            skLineSegment(sketch, "E45.right", {"start": v(-4.1, 0.9) * mm, "end": v(-4.1, 3.1) * mm});
            skSolve(sketch);
        }
        {
            var Q0;
            Q0=makeQuery(id+"F20.imprint","IMPRINT",FACE,{"disambiguationData":[TD([[makeQuery(id+"F20.imprint","IMPRINT",EDGE,{"derivedFrom":sQuery(id+"F20.wireOp",EDGE,"E40.bottom")}),-1.0]])]});
            var Q1;
            Q1=makeQuery(id+"F20.imprint","IMPRINT",FACE,{"disambiguationData":[TD([[makeQuery(id+"F20.imprint","IMPRINT",EDGE,{"derivedFrom":sQuery(id+"F20.wireOp",EDGE,"E40.bottom")}),1.0]])]});
            var Q2;
            Q2=makeQuery(id+"F1.opExtrude","SWEPT_BODY",BODY,{"disambiguationData":[OSD([sQuery(id+"F0.wireOp",EDGE,"E0"),sQuery(id+"F0.wireOp",EDGE,"E1.bottom"),sQuery(id+"F0.wireOp",EDGE,"E1.top"),sQuery(id+"F0.wireOp",EDGE,"E1.left"),sQuery(id+"F0.wireOp",EDGE,"E2"),sQuery(id+"F0.wireOp",EDGE,"E3"),sQuery(id+"F0.wireOp",EDGE,"E4"),sQuery(id+"F0.wireOp",EDGE,"E5")])]});
            extrude(context, id + "F21", {"entities" : qUnion([Q0, Q1]), "operationType" : NewBodyOperationType.ADD, "endBoundEntityBody" : qUnion([Q2]), "depth" : 3.5 * mm});
        }
        {
            var Q0;
            Q0=makeQuery(id+"F20.imprint","IMPRINT",FACE,{"disambiguationData":[TD([[makeQuery(id+"F20.imprint","IMPRINT",EDGE,{"derivedFrom":sQuery(id+"F20.wireOp",EDGE,"E40.bottom")}),1.0]])]});
            extrude(context, id + "F22", {"entities" : qUnion([Q0]), "operationType" : NewBodyOperationType.REMOVE, "endBound" : BoundingType.SYMMETRIC, "depth" : 1.5 * mm});
        }
        {
            var Q0;
            Q0=makeQuery(id+"F20.imprint","IMPRINT",FACE,{"disambiguationData":[TD([[makeQuery(id+"F20.imprint","IMPRINT",EDGE,{"derivedFrom":sQuery(id+"F20.wireOp",EDGE,"E44.bottom")}),-1.0]])]});
            var Q1;
            {var subQ0=sQuery(id+"F20.wireOp",EDGE,"E44.top");Q1=makeQuery(id+"F20.imprint","IMPRINT",FACE,{"disambiguationData":[TD([[makeQuery(id+"F20.imprint","IMPRINT",EDGE,{"derivedFrom":subQ0}),1.0]])]});}
            extrude(context, id + "F23", {"entities" : qUnion([Q0, Q1]), "operationType" : NewBodyOperationType.REMOVE, "depth" : 2.4 * mm});
        }
        {
            var Q0;
            {var subQ3=sQuery(id+"F11.wireOp",EDGE,"E34");Q0=makeQuery(id+"F11.imprint","IMPRINT",FACE,{"disambiguationData":[TD([[makeQuery(id+"F11.imprint","IMPRINT",EDGE,{"derivedFrom":subQ3}),1.0]])]});}
            extrude(context, id + "F24", {"entities" : qUnion([Q0]), "operationType" : NewBodyOperationType.REMOVE, "oppositeDirection" : true, "depth" : 19.1 * mm});
        }
        {
            var Q0;
            Q0=makeQuery(id+"F21.boolean.opBoolean","INTERSECT",EDGE,{"derivedFrom":[makeQuery(id+"F12.boolean.opBoolean","MERGE",FACE,{"derivedFrom":[makeQuery(id+"F1.opExtrude","SWEPT_FACE",FACE,{"disambiguationData":[OSD([sQuery(id+"F0.wireOp",EDGE,"E2")])]}),makeQuery(id+"F12.opExtrude","SWEPT_FACE",FACE,{"disambiguationData":[OSD([sQuery(id+"F11.wireOp",EDGE,"E33")])]})]}),makeQuery(id+"F21.opExtrude","SWEPT_FACE",FACE,{"disambiguationData":[OSD([sQuery(id+"F20.wireOp",EDGE,"E43.right")])]})]});
            var Q1;
            Q1=makeQuery(id+"F21.boolean.opBoolean","INTERSECT",EDGE,{"derivedFrom":[makeQuery(id+"F12.boolean.opBoolean","MERGE",FACE,{"derivedFrom":[makeQuery(id+"F1.opExtrude","SWEPT_FACE",FACE,{"disambiguationData":[OSD([sQuery(id+"F0.wireOp",EDGE,"E2")])]}),makeQuery(id+"F12.opExtrude","SWEPT_FACE",FACE,{"disambiguationData":[OSD([sQuery(id+"F11.wireOp",EDGE,"E33")])]})]}),makeQuery(id+"F21.opExtrude","SWEPT_FACE",FACE,{"disambiguationData":[OSD([sQuery(id+"F20.wireOp",EDGE,"E43.left")])]})]});
            fillet(context, id + "F25", {"entities" : qUnion([Q0, Q1]), "radius" : 10 * mm, "tangentPropagation" : true, "allowEdgeOverflow" : false});
        }
        {
            var Q0;
            Q0=makeQuery(id+"F14.opFillet","BLEND_EDGE",EDGE,{"blendedFrom":[makeQuery(id+"F13.opExtrude","CAP_EDGE",EDGE,{"disambiguationData":[OSD([sQuery(id+"F9.wireOp",EDGE,"E25.right")])],"isStart":false}),makeQuery(id+"F13.opExtrude","SWEPT_FACE",FACE,{"disambiguationData":[OSD([sQuery(id+"F9.wireOp",EDGE,"E25.bottom")])]})],"blendedInto":[makeQuery(id+"F13.opExtrude","SWEPT_FACE",FACE,{"disambiguationData":[OSD([sQuery(id+"F9.wireOp",EDGE,"E25.bottom")])]})]});
            var Q1;
            Q1=makeQuery(id+"F14.opFillet","BLEND_EDGE",EDGE,{"blendedFrom":[makeQuery(id+"F13.opExtrude","CAP_EDGE",EDGE,{"disambiguationData":[OSD([sQuery(id+"F9.wireOp",EDGE,"E30.MirrorCS")])],"isStart":false}),makeQuery(id+"F13.opExtrude","SWEPT_FACE",FACE,{"disambiguationData":[OSD([sQuery(id+"F9.wireOp",EDGE,"E28.MirrorCS")])]})],"blendedInto":[makeQuery(id+"F13.opExtrude","SWEPT_FACE",FACE,{"disambiguationData":[OSD([sQuery(id+"F9.wireOp",EDGE,"E28.MirrorCS")])]})]});
            var Q2;
            Q2=makeQuery(id+"F13.opExtrude","SWEPT_EDGE",EDGE,{"disambiguationData":[OSD([sQuery(id+"F9.wireOp",EDGE,"E25.bottom"),sQuery(id+"F9.wireOp",EDGE,"E25.right")])]});
            var Q3;
            Q3=makeQuery(id+"F13.opExtrude","SWEPT_EDGE",EDGE,{"disambiguationData":[OSD([sQuery(id+"F9.wireOp",EDGE,"E28.MirrorCS"),sQuery(id+"F9.wireOp",EDGE,"E31.MirrorCS")])]});
            var Q4;
            Q4=makeQuery(id+"F13.opExtrude","SWEPT_EDGE",EDGE,{"disambiguationData":[OSD([sQuery(id+"F9.wireOp",EDGE,"E28.MirrorCS"),sQuery(id+"F9.wireOp",EDGE,"E30.MirrorCS")])]});
            var Q5;
            Q5=makeQuery(id+"F13.opExtrude","SWEPT_EDGE",EDGE,{"disambiguationData":[OSD([sQuery(id+"F9.wireOp",EDGE,"E25.bottom"),sQuery(id+"F9.wireOp",EDGE,"E25.left")])]});
            var Q6;
            Q6=makeQuery(id+"F14.opFillet","BLEND_EDGE",EDGE,{"blendedFrom":[makeQuery(id+"F13.opExtrude","CAP_EDGE",EDGE,{"disambiguationData":[OSD([sQuery(id+"F9.wireOp",EDGE,"E25.left")])],"isStart":false}),makeQuery(id+"F13.opExtrude","SWEPT_FACE",FACE,{"disambiguationData":[OSD([sQuery(id+"F9.wireOp",EDGE,"E25.bottom")])]})],"blendedInto":[makeQuery(id+"F13.opExtrude","SWEPT_FACE",FACE,{"disambiguationData":[OSD([sQuery(id+"F9.wireOp",EDGE,"E25.bottom")])]})]});
            var Q7;
            Q7=makeQuery(id+"F13.opExtrude","CAP_EDGE",EDGE,{"disambiguationData":[OSD([sQuery(id+"F9.wireOp",EDGE,"E25.bottom")])],"isStart":false});
            var Q8;
            Q8=makeQuery(id+"F14.opFillet","BLEND_EDGE",EDGE,{"blendedFrom":[makeQuery(id+"F13.opExtrude","CAP_EDGE",EDGE,{"disambiguationData":[OSD([sQuery(id+"F9.wireOp",EDGE,"E31.MirrorCS")])],"isStart":false}),makeQuery(id+"F13.opExtrude","SWEPT_FACE",FACE,{"disambiguationData":[OSD([sQuery(id+"F9.wireOp",EDGE,"E28.MirrorCS")])]})],"blendedInto":[makeQuery(id+"F13.opExtrude","SWEPT_FACE",FACE,{"disambiguationData":[OSD([sQuery(id+"F9.wireOp",EDGE,"E28.MirrorCS")])]})]});
            var Q9;
            Q9=makeQuery(id+"F13.opExtrude","CAP_EDGE",EDGE,{"disambiguationData":[OSD([sQuery(id+"F9.wireOp",EDGE,"E28.MirrorCS")])],"isStart":false});
            fillet(context, id + "F26", {"entities" : qUnion([Q0, Q1, Q2, Q3, Q4, Q5, Q6, Q7, Q8, Q9]), "radius" : 6.46 * mm, "tangentPropagation" : true, "allowEdgeOverflow" : false});
        }
        {
            var Q0;
            Q0=makeQuery(id+"F1.opExtrude","CAP_EDGE",EDGE,{"disambiguationData":[OSD([sQuery(id+"F0.wireOp",EDGE,"E1.left")])],"isStart":false});
            var Q1;
            Q1=makeQuery(id+"F7.opExtrude","CAP_EDGE",EDGE,{"disambiguationData":[OSD([sQuery(id+"F6.wireOp",EDGE,"E20")])],"isStart":false});
            var Q2;
            Q2=makeQuery(id+"F1.opExtrude","CAP_EDGE",EDGE,{"disambiguationData":[OSD([sQuery(id+"F0.wireOp",EDGE,"E1.top")])],"isStart":false});
            var Q3;
            Q3=makeQuery(id+"F1.opExtrude","CAP_EDGE",EDGE,{"disambiguationData":[OSD([sQuery(id+"F0.wireOp",EDGE,"E1.bottom")])],"isStart":false});
            var Q4;
            Q4=makeQuery(id+"F7.opExtrude","CAP_EDGE",EDGE,{"disambiguationData":[OSD([sQuery(id+"F6.wireOp",EDGE,"E14")])],"isStart":true});
            var Q5;
            Q5=makeQuery(id+"F7.opExtrude","CAP_EDGE",EDGE,{"disambiguationData":[OSD([sQuery(id+"F6.wireOp",EDGE,"E13")])],"isStart":true});
            var Q6;
            Q6=makeQuery(id+"F7.opExtrude","CAP_EDGE",EDGE,{"disambiguationData":[OSD([sQuery(id+"F6.wireOp",EDGE,"E20")])],"isStart":true});
            var Q7;
            Q7=makeQuery(id+"F8.opExtrude","CAP_EDGE",EDGE,{"disambiguationData":[OSD([sQuery(id+"F6.wireOp",EDGE,"E13")])],"isStart":false});
            var Q8;
            Q8=makeQuery(id+"F8.opExtrude","CAP_EDGE",EDGE,{"disambiguationData":[OSD([sQuery(id+"F6.wireOp",EDGE,"E14")])],"isStart":false});
            var Q9;
            Q9=makeQuery(id+"F12.opExtrude","CAP_EDGE",EDGE,{"disambiguationData":[OSD([sQuery(id+"F11.wireOp",EDGE,"E33")])],"isStart":false});
            var Q10;
            Q10=makeQuery(id+"F7.opExtrude","CAP_EDGE",EDGE,{"disambiguationData":[OSD([sQuery(id+"F6.wireOp",EDGE,"E13")])],"isStart":false});
            var Q11;
            Q11=makeQuery(id+"F7.opExtrude","CAP_EDGE",EDGE,{"disambiguationData":[OSD([sQuery(id+"F6.wireOp",EDGE,"E14")])],"isStart":false});
            var Q12;
            Q12=makeQuery(id+"F7.opExtrude","CAP_EDGE",EDGE,{"disambiguationData":[OSD([sQuery(id+"F6.wireOp",EDGE,"E19")])],"isStart":false});
            var Q13;
            Q13=makeQuery(id+"F10.hole-0.boolean.opBoolean","INTERSECT",EDGE,{"derivedFrom":[makeQuery(id+"F8.boolean.opBoolean","SPLIT",FACE,{"disambiguationData":[TD([makeQuery(id+"F8.opExtrude","SWEPT_FACE",FACE,{"disambiguationData":[OSD([sQuery(id+"F6.wireOp",EDGE,"E20")])]})])],"derivedFrom":makeQuery(id+"F7.opExtrude","CAP_FACE",FACE,{"disambiguationData":[OSD([sQuery(id+"F6.wireOp",EDGE,"E11"),sQuery(id+"F6.wireOp",EDGE,"E12"),sQuery(id+"F6.wireOp",EDGE,"E13"),sQuery(id+"F6.wireOp",EDGE,"E14"),sQuery(id+"F6.wireOp",EDGE,"E19"),sQuery(id+"F6.wireOp",EDGE,"E22.bottom"),sQuery(id+"F6.wireOp",EDGE,"E22.top"),sQuery(id+"F6.wireOp",EDGE,"E22.left"),sQuery(id+"F6.wireOp",EDGE,"E23.bottom"),sQuery(id+"F6.wireOp",EDGE,"E23.top"),sQuery(id+"F6.wireOp",EDGE,"E23.left")])],"isStart":true})}),makeQuery(id+"F10.hole-0.opRevolve","SWEPT_FACE",FACE,{"disambiguationData":[OSD([sQuery(id+"F10.hole-0.sketch.wireOp",EDGE,"core_line_2")])]})]});
            var Q14;
            Q14=makeQuery(id+"F7.opExtrude","CAP_EDGE",EDGE,{"disambiguationData":[OSD([sQuery(id+"F6.wireOp",EDGE,"E23.left")])],"isStart":false});
            var Q15;
            Q15=makeQuery(id+"F7.opExtrude","CAP_EDGE",EDGE,{"disambiguationData":[OSD([sQuery(id+"F6.wireOp",EDGE,"E22.left")])],"isStart":false});
            fillet(context, id + "F27", {"entities" : qUnion([Q0, Q1, Q2, Q3, Q4, Q5, Q6, Q7, Q8, Q9, Q10, Q11, Q12, Q13, Q14, Q15]), "radius" : 0.5 * mm, "tangentPropagation" : true, "allowEdgeOverflow" : false});
        }
        {
            var Q0;
            Q0=makeQuery(id+"F26.opFillet","BLEND_EDGE",EDGE,{"disambiguationData":[OD(0.0)],"blendedFrom":[makeQuery(id+"F13.opExtrude","SWEPT_EDGE",EDGE,{"disambiguationData":[OSD([sQuery(id+"F9.wireOp",EDGE,"E25.bottom"),sQuery(id+"F9.wireOp",EDGE,"E25.right")])]}),makeQuery(id+"F13.opExtrude","SWEPT_FACE",FACE,{"disambiguationData":[OSD([sQuery(id+"F9.wireOp",EDGE,"E25.top")])]})],"blendedInto":[makeQuery(id+"F13.opExtrude","SWEPT_FACE",FACE,{"disambiguationData":[OSD([sQuery(id+"F9.wireOp",EDGE,"E25.top")])]})]});
            var Q1;
            Q1=makeQuery(id+"F26.opFillet","BLEND_EDGE",EDGE,{"disambiguationData":[OD(0.0)],"blendedFrom":[makeQuery(id+"F13.opExtrude","SWEPT_EDGE",EDGE,{"disambiguationData":[OSD([sQuery(id+"F9.wireOp",EDGE,"E28.MirrorCS"),sQuery(id+"F9.wireOp",EDGE,"E30.MirrorCS")])]}),makeQuery(id+"F13.opExtrude","SWEPT_FACE",FACE,{"disambiguationData":[OSD([sQuery(id+"F9.wireOp",EDGE,"E29.MirrorCS")])]})],"blendedInto":[makeQuery(id+"F13.opExtrude","SWEPT_FACE",FACE,{"disambiguationData":[OSD([sQuery(id+"F9.wireOp",EDGE,"E29.MirrorCS")])]})]});
            fillet(context, id + "F28", {"entities" : qUnion([Q0, Q1]), "radius" : 0.5 * mm, "tangentPropagation" : true, "allowEdgeOverflow" : false});
        }
        {
            var Q0;
            Q0=makeQuery(id+"F13.opExtrude","SWEPT_FACE",FACE,{"disambiguationData":[OSD([sQuery(id+"F9.wireOp",EDGE,"E29.MirrorCS")])]});
            var sketch = newSketch(context, id + "F29", { "sketchPlane" : qUnion([Q0])});
            skPoint(sketch, "E46", {"position": v(0, 32) * mm});
            skSolve(sketch);
        }
        {
            var Q0;
            Q0=makeQuery(id+"F13.opExtrude","SWEPT_FACE",FACE,{"disambiguationData":[OSD([sQuery(id+"F9.wireOp",EDGE,"E25.top")])]});
            var sketch = newSketch(context, id + "F30", { "sketchPlane" : qUnion([Q0])});
            skPoint(sketch, "E47", {"position": v(0, 32) * mm});
            skSolve(sketch);
        }
        {
            var Q0;
            Q0=sQuery(id+"F30.wireOp",VERTEX,"E47");
            var Q1;
            Q1=sQuery(id+"F29.wireOp",VERTEX,"E46");
            var Q2;
            Q2=makeQuery(id+"F7.opExtrude","SWEPT_BODY",BODY,{"disambiguationData":[OSD([sQuery(id+"F6.wireOp",EDGE,"E11"),sQuery(id+"F6.wireOp",EDGE,"E12"),sQuery(id+"F6.wireOp",EDGE,"E13"),sQuery(id+"F6.wireOp",EDGE,"E14"),sQuery(id+"F6.wireOp",EDGE,"E17"),sQuery(id+"F6.wireOp",EDGE,"E18"),sQuery(id+"F6.wireOp",EDGE,"E20")])]});
            hole(context, id + "F31", {"style" : HoleStyle.SIMPLE, "endStyle" : HoleEndStyle.BLIND, "holeDiameter" : 2 * mm, "holeDepth" : 2 * mm, "locations" : qUnion([Q0, Q1]), "scope" : qUnion([Q2])});
        }
    });
